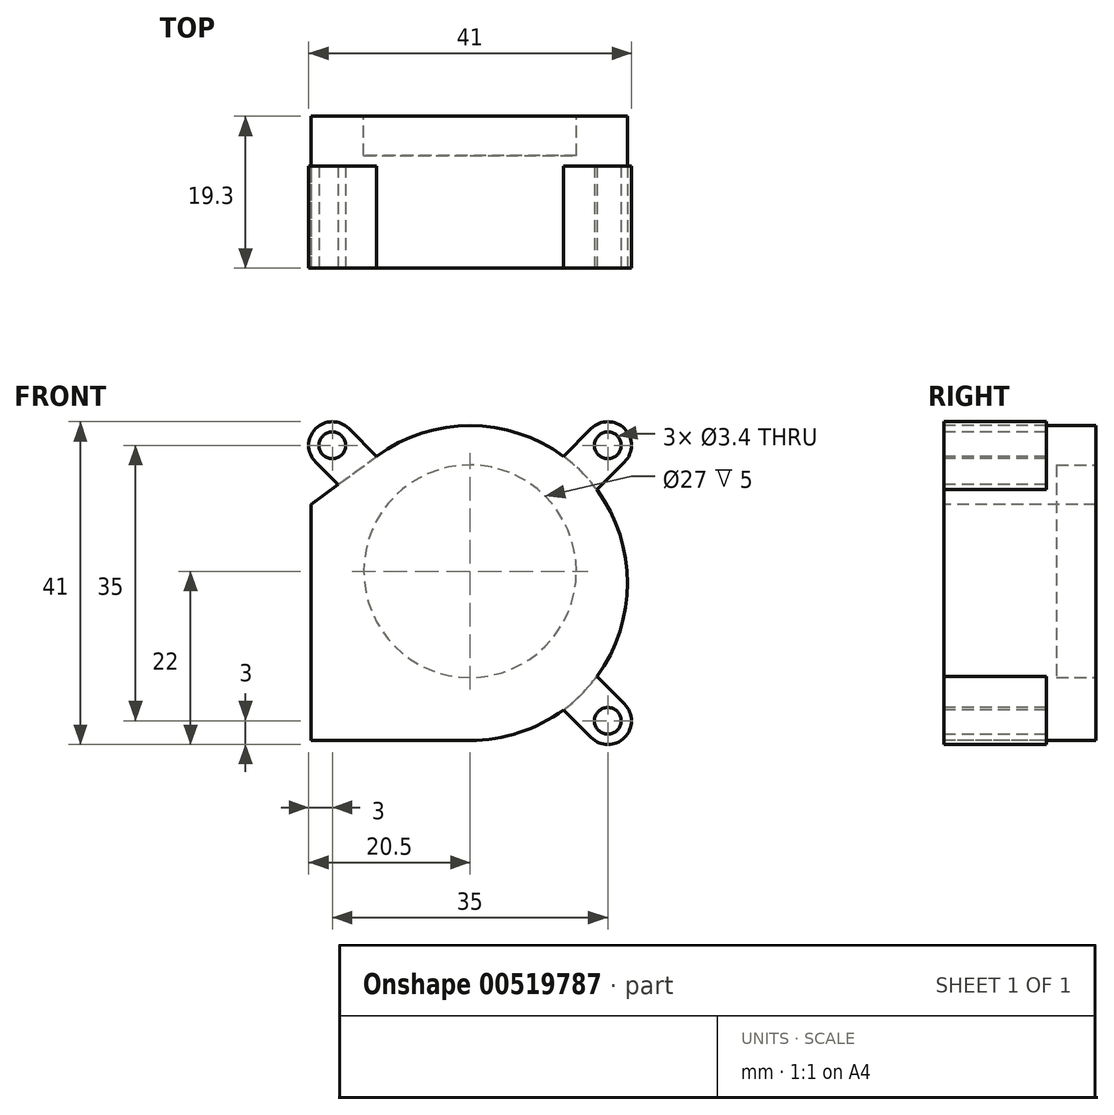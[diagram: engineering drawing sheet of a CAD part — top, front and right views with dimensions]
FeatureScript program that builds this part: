
annotation { "Feature Type Name" : "Feature", "Feature Type Description" : "" }
export const myFeature = defineFeature(function(context is Context, id is Id, definition is map)
    precondition{}
    {
        {
            var Q0;
            Q0=qCreatedBy(makeId("Front.planeOp"),FACE);
            var sketch = newSketch(context, id + "F0", { "sketchPlane" : qUnion([Q0])});
            skArc(sketch, "E0", {"start": v(0, -20) * mm, "mid": v(19.01, 6.21) * mm, "end": v(-11.81, 16.14) * mm});
            skLineSegment(sketch, "E1", {"start": v(0, -20) * mm, "end": v(-20.2, -20) * mm});
            skLineSegment(sketch, "E2", {"start": v(-20.2, -20) * mm, "end": v(-20.2, 10) * mm});
            skLineSegment(sketch, "E3", {"start": v(-20.2, 10) * mm, "end": v(-11.81, 16.14) * mm});
            skLineSegment(sketch, "E4.bottom", {"start": v(-17.5, 17.5) * mm, "end": v(17.5, 17.5) * mm, "construction": true});
            skLineSegment(sketch, "E4.top", {"start": v(-17.5, -17.5) * mm, "end": v(17.5, -17.5) * mm, "construction": true});
            skLineSegment(sketch, "E4.left", {"start": v(-17.5, 17.5) * mm, "end": v(-17.5, -17.5) * mm, "construction": true});
            skLineSegment(sketch, "E4.right", {"start": v(17.5, 17.5) * mm, "end": v(17.5, -17.5) * mm, "construction": true});
            skCircle(sketch, "E5", {"center": v(-17.5, 17.5) * mm, "radius": 1.7 * mm});
            skCircle(sketch, "E6", {"center": v(17.5, -17.5) * mm, "radius": 1.7 * mm});
            skArc(sketch, "E7", {"start": v(15.38, 19.62) * mm, "mid": v(19.62, 19.62) * mm, "end": v(19.62, 15.38) * mm});
            skLineSegment(sketch, "E8", {"start": v(15.38, 19.62) * mm, "end": v(19.62, 15.38) * mm, "construction": true});
            skLineSegment(sketch, "E9", {"start": v(15.38, 19.62) * mm, "end": v(11.86, 16.1) * mm});
            skLineSegment(sketch, "E10", {"start": v(19.62, 15.38) * mm, "end": v(16.1, 11.86) * mm});
            skLineSegment(sketch, "E11.MirrorCS", {"start": v(15.38, -19.62) * mm, "end": v(19.62, -15.38) * mm, "construction": true});
            skLineSegment(sketch, "E12.MirrorCS", {"start": v(15.38, -19.62) * mm, "end": v(11.86, -16.1) * mm});
            skLineSegment(sketch, "E13.MirrorCS", {"start": v(19.62, -15.38) * mm, "end": v(16.1, -11.86) * mm});
            skArc(sketch, "E14.MirrorCS", {"start": v(15.38, -19.62) * mm, "mid": v(19.62, -19.62) * mm, "end": v(19.62, -15.38) * mm});
            skCircle(sketch, "E15.MirrorC", {"center": v(17.5, 17.5) * mm, "radius": 1.7 * mm});
            skLineSegment(sketch, "E16.MirrorCS", {"start": v(-15.38, 19.62) * mm, "end": v(-11.86, 16.1) * mm});
            skArc(sketch, "E17.MirrorCS", {"start": v(-15.38, 19.62) * mm, "mid": v(-19.62, 19.62) * mm, "end": v(-19.62, 15.38) * mm});
            skLineSegment(sketch, "E18.MirrorCS", {"start": v(-19.62, 15.38) * mm, "end": v(-16.1, 11.86) * mm});
            skSolve(sketch);
        }
        {
            var Q0;
            Q0 = qSketchRegion(id + "F0", true);
            extrude(context, id + "F1", {"entities" : qUnion([Q0]), "oppositeDirection" : true, "depth" : 13 * mm, "offsetDistance" : 25 * mm});
        }
        {
            var Q0;
            {var subQ5=sQuery(id+"F0.wireOp",EDGE,"E1");Q0=makeQuery(id+"F0.imprint","IMPRINT",FACE,{"disambiguationData":[TD([[makeQuery(id+"F0.imprint","IMPRINT",EDGE,{"derivedFrom":subQ5}),-1.0]])]});}
            extrude(context, id + "F2", {"entities" : qUnion([Q0]), "operationType" : NewBodyOperationType.ADD, "oppositeDirection" : true, "depth" : 19.3 * mm, "offsetDistance" : 25 * mm});
        }
        {
            var Q0;
            Q0=makeQuery(id+"F2.opExtrude","CAP_FACE",FACE,{"disambiguationData":[OSD([sQuery(id+"F0.wireOp",EDGE,"E0"),sQuery(id+"F0.wireOp",EDGE,"E1"),sQuery(id+"F0.wireOp",EDGE,"E2"),sQuery(id+"F0.wireOp",EDGE,"E3")])],"isStart":false});
            var sketch = newSketch(context, id + "F3", { "sketchPlane" : qUnion([Q0])});
            skCircle(sketch, "E19", {"center": v(0, 1.5) * mm, "radius": 13.5 * mm});
            skSolve(sketch);
        }
        {
            var Q0;
            Q0 = qSketchRegion(id + "F3", true);
            extrude(context, id + "F4", {"entities" : qUnion([Q0]), "operationType" : NewBodyOperationType.REMOVE, "oppositeDirection" : true, "depth" : 5 * mm, "offsetDistance" : 25 * mm});
        }
    });
